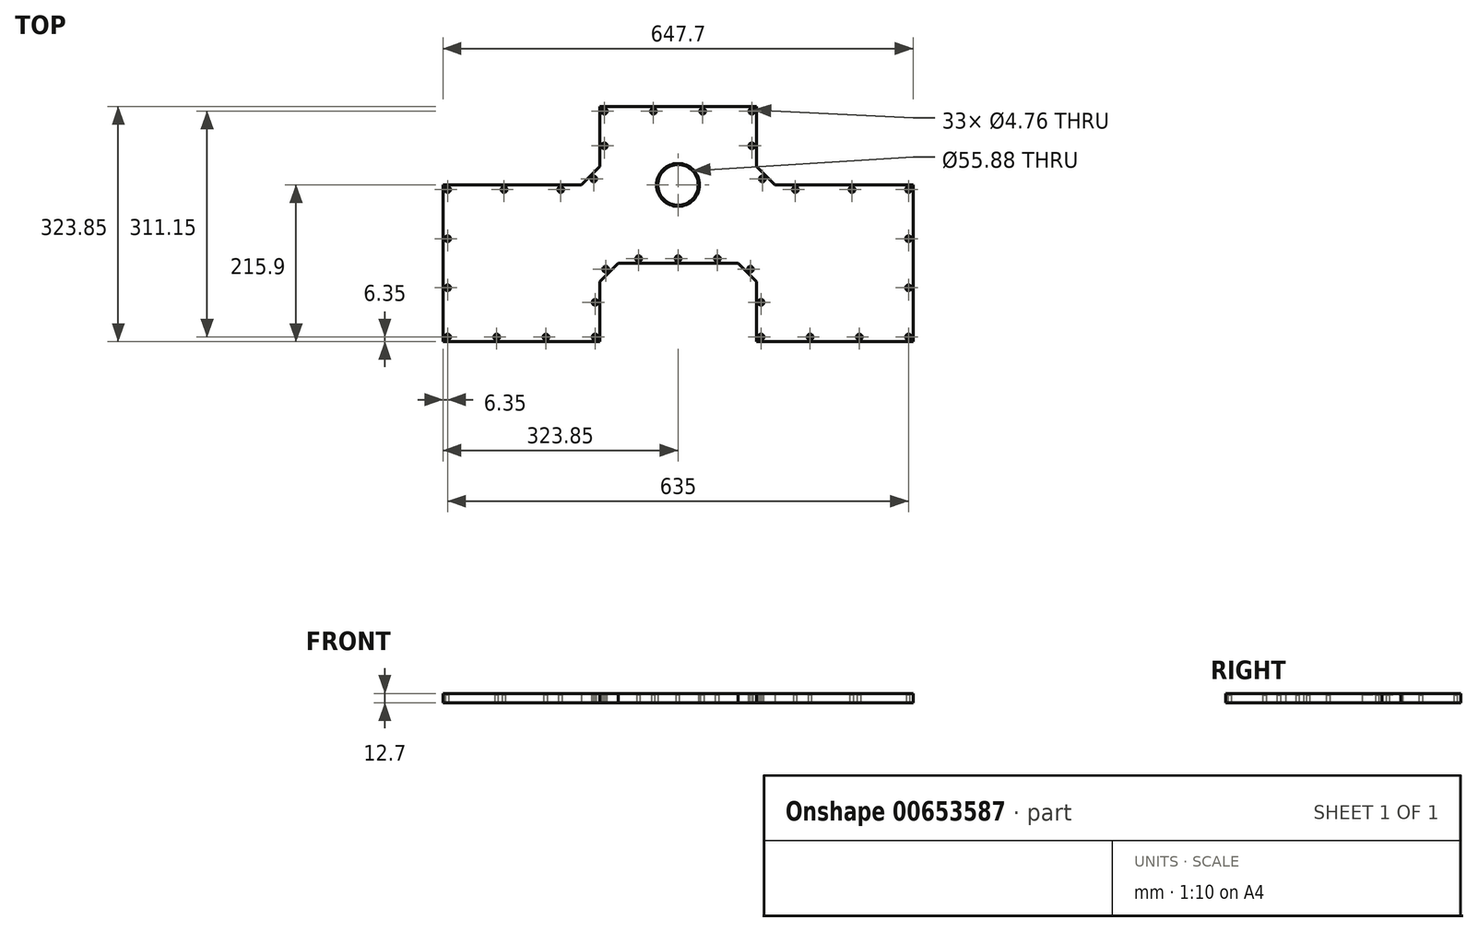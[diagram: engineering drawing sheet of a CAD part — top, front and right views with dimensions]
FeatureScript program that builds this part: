
annotation { "Feature Type Name" : "Feature", "Feature Type Description" : "" }
export const myFeature = defineFeature(function(context is Context, id is Id, definition is map)
    precondition{}
    {
        {
            var Q0;
            Q0=qCreatedBy(makeId("Top.planeOp"),FACE);
            var sketch = newSketch(context, id + "F0", { "sketchPlane" : qUnion([Q0])});
            skLineSegment(sketch, "E0.bottom", {"start": v(82.55, 0) * mm, "end": v(-82.55, 0) * mm});
            skLineSegment(sketch, "E0.top", {"start": v(107.95, 215.9) * mm, "end": v(-107.95, 215.9) * mm});
            skPoint(sketch, "E0.middle", {"position": v(0, 107.95) * mm});
            skLineSegment(sketch, "E1.bottom", {"start": v(133.35, 107.95) * mm, "end": v(323.85, 107.95) * mm});
            skLineSegment(sketch, "E1.top", {"start": v(107.95, -107.95) * mm, "end": v(323.85, -107.95) * mm});
            skLineSegment(sketch, "E1.left", {"start": v(107.95, -25.4) * mm, "end": v(107.95, -107.95) * mm});
            skLineSegment(sketch, "E1.right", {"start": v(323.85, 107.95) * mm, "end": v(323.85, -107.95) * mm});
            skPoint(sketch, "E1.middle", {"position": v(215.9, 0) * mm});
            skLineSegment(sketch, "E2.bottom", {"start": v(-133.35, 107.95) * mm, "end": v(-323.85, 107.95) * mm});
            skLineSegment(sketch, "E2.top", {"start": v(-107.95, -107.95) * mm, "end": v(-323.85, -107.95) * mm});
            skLineSegment(sketch, "E2.right", {"start": v(-323.85, 107.95) * mm, "end": v(-323.85, -107.95) * mm});
            skPoint(sketch, "E2.middle", {"position": v(-215.9, 0) * mm});
            skLineSegment(sketch, "E3", {"start": v(82.55, 0) * mm, "end": v(107.95, -25.4) * mm});
            skLineSegment(sketch, "E4", {"start": v(-82.55, 0) * mm, "end": v(-107.95, -25.4) * mm});
            skLineSegment(sketch, "E5", {"start": v(-107.95, 133.35) * mm, "end": v(-133.35, 107.95) * mm});
            skLineSegment(sketch, "E6", {"start": v(133.35, 107.95) * mm, "end": v(107.95, 133.35) * mm});
            skLineSegment(sketch, "E7.trimOffspring", {"start": v(107.95, 133.35) * mm, "end": v(107.95, 215.9) * mm});
            skPoint(sketch, "E0.left.end.orphan", {"position": v(107.95, 107.95) * mm});
            skPoint(sketch, "E0.left.start.orphan", {"position": v(107.95, 0) * mm});
            skLineSegment(sketch, "E8.trimOffspring", {"start": v(-107.95, -25.4) * mm, "end": v(-107.95, -107.95) * mm});
            skPoint(sketch, "E9.orphan", {"position": v(-107.95, 107.95) * mm});
            skLineSegment(sketch, "E10.trimOffspring", {"start": v(-107.95, 133.35) * mm, "end": v(-107.95, 215.9) * mm});
            skPoint(sketch, "E0.right.start.orphan", {"position": v(-107.95, 0) * mm});
            skLineSegment(sketch, "E11", {"start": v(-107.95, 133.35) * mm, "end": v(-107.95, 0) * mm, "construction": true});
            skLineSegment(sketch, "E12", {"start": v(-82.55, 0) * mm, "end": v(-107.95, 0) * mm, "construction": true});
            skLineSegment(sketch, "E13", {"start": v(82.55, 0) * mm, "end": v(107.95, 0) * mm, "construction": true});
            skLineSegment(sketch, "E14", {"start": v(107.95, 0) * mm, "end": v(107.95, 133.35) * mm, "construction": true});
            skLineSegment(sketch, "E15", {"start": v(133.35, 107.95) * mm, "end": v(107.95, 107.95) * mm, "construction": true});
            skLineSegment(sketch, "E16", {"start": v(107.95, 107.95) * mm, "end": v(107.95, -25.4) * mm, "construction": true});
            skLineSegment(sketch, "E17", {"start": v(-133.35, 107.95) * mm, "end": v(-107.95, 107.95) * mm, "construction": true});
            skLineSegment(sketch, "E18", {"start": v(-107.95, 107.95) * mm, "end": v(-107.95, -25.4) * mm, "construction": true});
            skCircle(sketch, "E19", {"center": v(0, 107.95) * mm, "radius": 27.94 * mm});
            skSolve(sketch);
        }
        {
            var Q0;
            Q0=makeQuery(id+"F0.imprint","IMPRINT",FACE,{"disambiguationData":[TD([[makeQuery(id+"F0.imprint","IMPRINT",EDGE,{"derivedFrom":sQuery(id+"F0.wireOp",EDGE,"E0.bottom")}),-1.0]])]});
            extrude(context, id + "F1", {"entities" : qUnion([Q0]), "depth" : 12.7 * mm, "offsetDistance" : 25.4 * mm});
        }
        {
            var Q0;
            Q0=makeQuery(id+"F1.opExtrude","CAP_FACE",FACE,{"disambiguationData":[OSD([sQuery(id+"F0.wireOp",EDGE,"E0.bottom"),sQuery(id+"F0.wireOp",EDGE,"E0.top"),sQuery(id+"F0.wireOp",EDGE,"E1.bottom"),sQuery(id+"F0.wireOp",EDGE,"E1.top"),sQuery(id+"F0.wireOp",EDGE,"E1.left"),sQuery(id+"F0.wireOp",EDGE,"E1.right"),sQuery(id+"F0.wireOp",EDGE,"E2.bottom"),sQuery(id+"F0.wireOp",EDGE,"E2.top"),sQuery(id+"F0.wireOp",EDGE,"E2.right"),sQuery(id+"F0.wireOp",EDGE,"QcSHtbIY-mSPd-EMcu-2M9r-5KKswnyoFa2N"),sQuery(id+"F0.wireOp",EDGE,"raY0HwxW-YMRD-rCHu-SJPv-7X02aoJlrJC0"),sQuery(id+"F0.wireOp",EDGE,"ysclZKg7-ktj4-C8mT-U7f8-jFngsUPYq0i9"),sQuery(id+"F0.wireOp",EDGE,"E3"),sQuery(id+"F0.wireOp",EDGE,"E4"),sQuery(id+"F0.wireOp",EDGE,"E5"),sQuery(id+"F0.wireOp",EDGE,"E6"),sQuery(id+"F0.wireOp",EDGE,"E7.trimOffspring"),sQuery(id+"F0.wireOp",EDGE,"E8.trimOffspring"),sQuery(id+"F0.wireOp",EDGE,"E10.trimOffspring")])],"isStart":false});
            var sketch = newSketch(context, id + "F2", { "sketchPlane" : qUnion([Q0])});
            skLineSegment(sketch, "E20.0", {"start": v(317.5, 101.6) * mm, "end": v(130.72, 101.6) * mm});
            skLineSegment(sketch, "E20.1", {"start": v(317.5, -101.6) * mm, "end": v(317.5, 101.6) * mm});
            skLineSegment(sketch, "E20.2", {"start": v(114.3, -101.6) * mm, "end": v(317.5, -101.6) * mm});
            skLineSegment(sketch, "E20.3", {"start": v(114.3, -22.77) * mm, "end": v(114.3, -101.6) * mm});
            skLineSegment(sketch, "E20.4", {"start": v(85.18, 6.35) * mm, "end": v(114.3, -22.77) * mm});
            skLineSegment(sketch, "E20.5", {"start": v(-101.6, 130.72) * mm, "end": v(-130.72, 101.6) * mm});
            skLineSegment(sketch, "E20.6", {"start": v(-101.6, 209.55) * mm, "end": v(-101.6, 130.72) * mm});
            skLineSegment(sketch, "E20.7", {"start": v(101.6, 209.55) * mm, "end": v(-101.6, 209.55) * mm});
            skLineSegment(sketch, "E20.8", {"start": v(101.6, 130.72) * mm, "end": v(101.6, 209.55) * mm});
            skLineSegment(sketch, "E20.9", {"start": v(-130.72, 101.6) * mm, "end": v(-317.5, 101.6) * mm});
            skLineSegment(sketch, "E20.10", {"start": v(-317.5, 101.6) * mm, "end": v(-317.5, -101.6) * mm});
            skLineSegment(sketch, "E20.11", {"start": v(-317.5, -101.6) * mm, "end": v(-114.3, -101.6) * mm});
            skLineSegment(sketch, "E20.12", {"start": v(-114.3, -101.6) * mm, "end": v(-114.3, -22.77) * mm});
            skLineSegment(sketch, "E20.13", {"start": v(-114.3, -22.77) * mm, "end": v(-85.18, 6.35) * mm});
            skLineSegment(sketch, "E20.14", {"start": v(130.72, 101.6) * mm, "end": v(101.6, 130.72) * mm});
            skLineSegment(sketch, "E20.15", {"start": v(-85.18, 6.35) * mm, "end": v(85.18, 6.35) * mm});
            skPoint(sketch, "E21", {"position": v(-33.87, 209.55) * mm});
            skPoint(sketch, "E22", {"position": v(33.87, 209.55) * mm});
            skPoint(sketch, "E23", {"position": v(116.16, 116.16) * mm});
            skPoint(sketch, "E24", {"position": v(-116.16, 116.16) * mm});
            skPoint(sketch, "E25", {"position": v(-161.72, 101.6) * mm});
            skPoint(sketch, "E26", {"position": v(-239.6, 101.6) * mm});
            skPoint(sketch, "E27", {"position": v(-317.5, 33.87) * mm});
            skPoint(sketch, "E28", {"position": v(-317.5, -33.87) * mm});
            skPoint(sketch, "E29", {"position": v(-249.77, -101.6) * mm});
            skPoint(sketch, "E30", {"position": v(-182.03, -101.6) * mm});
            skPoint(sketch, "E31", {"position": v(-114.3, -53.77) * mm});
            skPoint(sketch, "E32", {"position": v(-99.74, -8.2) * mm});
            skPoint(sketch, "E33", {"position": v(-54.18, 6.35) * mm});
            skPoint(sketch, "E34", {"position": v(54.18, 6.35) * mm});
            skPoint(sketch, "E35", {"position": v(99.74, -8.2) * mm});
            skPoint(sketch, "E36", {"position": v(114.3, -53.77) * mm});
            skPoint(sketch, "E37", {"position": v(182.03, -101.6) * mm});
            skPoint(sketch, "E38", {"position": v(249.77, -101.6) * mm});
            skPoint(sketch, "E39", {"position": v(317.5, -33.87) * mm});
            skPoint(sketch, "E40", {"position": v(317.5, 33.87) * mm});
            skPoint(sketch, "E41", {"position": v(239.6, 101.6) * mm});
            skPoint(sketch, "E42", {"position": v(161.72, 101.6) * mm});
            skPoint(sketch, "E43", {"position": v(101.6, 161.72) * mm});
            skPoint(sketch, "E44", {"position": v(-101.6, 161.72) * mm});
            skLineSegment(sketch, "E45", {"start": v(-101.6, 161.72) * mm, "end": v(-116.16, 116.16) * mm, "construction": true});
            skLineSegment(sketch, "E46", {"start": v(-116.16, 116.16) * mm, "end": v(-161.72, 101.6) * mm, "construction": true});
            skLineSegment(sketch, "E47", {"start": v(-99.74, -8.2) * mm, "end": v(-54.18, 6.35) * mm, "construction": true});
            skLineSegment(sketch, "E48", {"start": v(-99.74, -8.2) * mm, "end": v(-114.3, -53.77) * mm, "construction": true});
            skLineSegment(sketch, "E49", {"start": v(99.74, -8.2) * mm, "end": v(54.18, 6.35) * mm, "construction": true});
            skLineSegment(sketch, "E50", {"start": v(99.74, -8.2) * mm, "end": v(114.3, -53.77) * mm, "construction": true});
            skLineSegment(sketch, "E51", {"start": v(116.16, 116.16) * mm, "end": v(161.72, 101.6) * mm, "construction": true});
            skLineSegment(sketch, "E52", {"start": v(116.16, 116.16) * mm, "end": v(101.6, 161.72) * mm, "construction": true});
            skLineSegment(sketch, "E53", {"start": v(-101.6, 161.72) * mm, "end": v(-101.6, 209.55) * mm, "construction": true});
            skLineSegment(sketch, "E54", {"start": v(-101.6, 209.55) * mm, "end": v(-33.87, 209.55) * mm, "construction": true});
            skLineSegment(sketch, "E55", {"start": v(-33.87, 209.55) * mm, "end": v(33.87, 209.55) * mm, "construction": true});
            skLineSegment(sketch, "E56", {"start": v(33.87, 209.55) * mm, "end": v(101.6, 209.55) * mm, "construction": true});
            skLineSegment(sketch, "E57", {"start": v(-161.72, 101.6) * mm, "end": v(-239.6, 101.6) * mm, "construction": true});
            skLineSegment(sketch, "E58", {"start": v(-239.6, 101.6) * mm, "end": v(-317.5, 101.6) * mm, "construction": true});
            skLineSegment(sketch, "E59", {"start": v(-317.5, 101.6) * mm, "end": v(-317.5, 33.87) * mm, "construction": true});
            skLineSegment(sketch, "E60", {"start": v(-317.5, 33.87) * mm, "end": v(-317.5, -33.87) * mm, "construction": true});
            skLineSegment(sketch, "E61", {"start": v(-317.5, -33.87) * mm, "end": v(-317.5, -101.6) * mm, "construction": true});
            skLineSegment(sketch, "E62", {"start": v(-317.5, -101.6) * mm, "end": v(-249.77, -101.6) * mm, "construction": true});
            skLineSegment(sketch, "E63", {"start": v(-249.77, -101.6) * mm, "end": v(-182.03, -101.6) * mm, "construction": true});
            skLineSegment(sketch, "E64", {"start": v(-182.03, -101.6) * mm, "end": v(-114.3, -101.6) * mm, "construction": true});
            skPoint(sketch, "E65", {"position": v(0, 6.35) * mm});
            skLineSegment(sketch, "E66", {"start": v(161.72, 101.6) * mm, "end": v(239.6, 101.6) * mm, "construction": true});
            skLineSegment(sketch, "E67", {"start": v(239.6, 101.6) * mm, "end": v(317.5, 101.6) * mm, "construction": true});
            skLineSegment(sketch, "E68", {"start": v(317.5, 101.6) * mm, "end": v(317.5, 33.87) * mm, "construction": true});
            skLineSegment(sketch, "E69", {"start": v(317.5, 33.87) * mm, "end": v(317.5, -33.87) * mm, "construction": true});
            skLineSegment(sketch, "E70", {"start": v(317.5, -33.87) * mm, "end": v(317.5, -101.6) * mm, "construction": true});
            skLineSegment(sketch, "E71", {"start": v(317.5, -101.6) * mm, "end": v(249.77, -101.6) * mm, "construction": true});
            skLineSegment(sketch, "E72", {"start": v(249.77, -101.6) * mm, "end": v(182.03, -101.6) * mm, "construction": true});
            skLineSegment(sketch, "E73", {"start": v(182.03, -101.6) * mm, "end": v(114.3, -101.6) * mm, "construction": true});
            skSolve(sketch);
        }
        {
            var Q0;
            Q0=sQuery(id+"F2.wireOp",VERTEX,"E26");
            var Q1;
            Q1=sQuery(id+"F2.wireOp",VERTEX,"E25");
            var Q2;
            Q2=sQuery(id+"F2.wireOp",VERTEX,"E24");
            var Q3;
            Q3=sQuery(id+"F2.wireOp",VERTEX,"E44");
            var Q4;
            Q4=sQuery(id+"F2.wireOp",VERTEX,"E20.6.start");
            var Q5;
            Q5=sQuery(id+"F2.wireOp",VERTEX,"E21");
            var Q6;
            Q6=sQuery(id+"F2.wireOp",VERTEX,"E22");
            var Q7;
            Q7=sQuery(id+"F2.wireOp",VERTEX,"E20.7.start");
            var Q8;
            Q8=sQuery(id+"F2.wireOp",VERTEX,"E43");
            var Q9;
            Q9=sQuery(id+"F2.wireOp",VERTEX,"E23");
            var Q10;
            Q10=sQuery(id+"F2.wireOp",VERTEX,"E42");
            var Q11;
            Q11=sQuery(id+"F2.wireOp",VERTEX,"E41");
            var Q12;
            Q12=sQuery(id+"F2.wireOp",VERTEX,"E40");
            var Q13;
            Q13=sQuery(id+"F2.wireOp",VERTEX,"E20.0.start");
            var Q14;
            Q14=sQuery(id+"F2.wireOp",VERTEX,"E39");
            var Q15;
            Q15=sQuery(id+"F2.wireOp",VERTEX,"E20.2.end");
            var Q16;
            Q16=sQuery(id+"F2.wireOp",VERTEX,"E38");
            var Q17;
            Q17=sQuery(id+"F2.wireOp",VERTEX,"E37");
            var Q18;
            Q18=sQuery(id+"F2.wireOp",VERTEX,"E36");
            var Q19;
            Q19=sQuery(id+"F2.wireOp",VERTEX,"E20.3.end");
            var Q20;
            Q20=sQuery(id+"F2.wireOp",VERTEX,"E35");
            var Q21;
            Q21=sQuery(id+"F2.wireOp",VERTEX,"E34");
            var Q22;
            Q22=sQuery(id+"F2.wireOp",VERTEX,"E65");
            var Q23;
            Q23=sQuery(id+"F2.wireOp",VERTEX,"E33");
            var Q24;
            Q24=sQuery(id+"F2.wireOp",VERTEX,"E32");
            var Q25;
            Q25=sQuery(id+"F2.wireOp",VERTEX,"E31");
            var Q26;
            Q26=sQuery(id+"F2.wireOp",VERTEX,"E20.12.start");
            var Q27;
            Q27=sQuery(id+"F2.wireOp",VERTEX,"E30");
            var Q28;
            Q28=sQuery(id+"F2.wireOp",VERTEX,"E29");
            var Q29;
            Q29=sQuery(id+"F2.wireOp",VERTEX,"E62.start");
            var Q30;
            Q30=sQuery(id+"F2.wireOp",VERTEX,"E28");
            var Q31;
            Q31=sQuery(id+"F2.wireOp",VERTEX,"E27");
            var Q32;
            Q32=sQuery(id+"F2.wireOp",VERTEX,"E20.10.start");
            var Q33;
            Q33=makeQuery(id+"F1.opExtrude","SWEPT_BODY",BODY,{"disambiguationData":[OSD([sQuery(id+"F0.wireOp",EDGE,"E0.bottom"),sQuery(id+"F0.wireOp",EDGE,"E0.top"),sQuery(id+"F0.wireOp",EDGE,"E1.bottom"),sQuery(id+"F0.wireOp",EDGE,"E1.top"),sQuery(id+"F0.wireOp",EDGE,"E1.left"),sQuery(id+"F0.wireOp",EDGE,"E1.right"),sQuery(id+"F0.wireOp",EDGE,"E2.bottom"),sQuery(id+"F0.wireOp",EDGE,"E2.top"),sQuery(id+"F0.wireOp",EDGE,"E2.right"),sQuery(id+"F0.wireOp",EDGE,"QcSHtbIY-mSPd-EMcu-2M9r-5KKswnyoFa2N"),sQuery(id+"F0.wireOp",EDGE,"raY0HwxW-YMRD-rCHu-SJPv-7X02aoJlrJC0"),sQuery(id+"F0.wireOp",EDGE,"ysclZKg7-ktj4-C8mT-U7f8-jFngsUPYq0i9"),sQuery(id+"F0.wireOp",EDGE,"E3"),sQuery(id+"F0.wireOp",EDGE,"E4"),sQuery(id+"F0.wireOp",EDGE,"E5"),sQuery(id+"F0.wireOp",EDGE,"E6"),sQuery(id+"F0.wireOp",EDGE,"E7.trimOffspring"),sQuery(id+"F0.wireOp",EDGE,"E8.trimOffspring"),sQuery(id+"F0.wireOp",EDGE,"E10.trimOffspring")])]});
            hole(context, id + "F3", {"style" : HoleStyle.C_SINK, "endStyle" : HoleEndStyle.THROUGH, "holeDiameter" : 4.76 * mm, "cSinkDiameter" : 7.94 * mm, "cSinkAngle" : 85 * degree, "majorDiameter" : 6.35 * mm, "isTappedThrough" : true, "tappedDepth" : 12.7 * mm, "tapClearance" : 3, "locations" : qUnion([Q0, Q1, Q2, Q3, Q4, Q5, Q6, Q7, Q8, Q9, Q10, Q11, Q12, Q13, Q14, Q15, Q16, Q17, Q18, Q19, Q20, Q21, Q22, Q23, Q24, Q25, Q26, Q27, Q28, Q29, Q30, Q31, Q32]), "scope" : qUnion([Q33])});
        }
        {
            var Q0;
            Q0=makeQuery(id+"F1.opExtrude","CAP_EDGE",EDGE,{"disambiguationData":[OSD([sQuery(id+"F0.wireOp",EDGE,"E19")])],"isStart":false});
            chamfer(context, id + "F4", {"entities" : qUnion([Q0]), "width" : 1.59 * mm, "tangentPropagation" : true});
        }
    });
